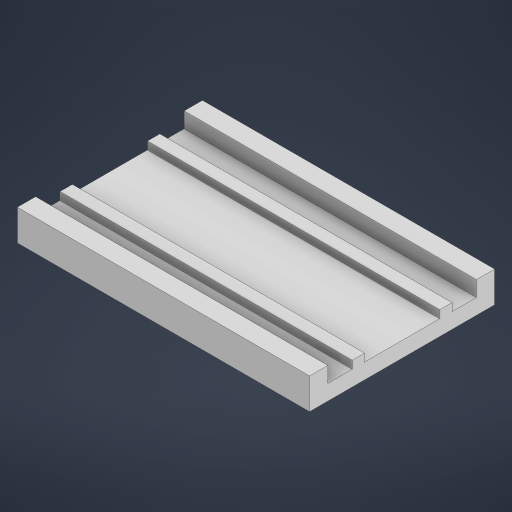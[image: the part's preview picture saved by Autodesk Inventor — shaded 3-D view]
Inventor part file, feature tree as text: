
AUTODESK INVENTOR PART (.ipt)
format: ipt  version: 2024 (Build 280153000, 153)  size: 219,648 bytes
history: native  units: in
note: dims shown in document units (in); Inventor stores cm internally (conversion verified against a paired STEP export)
features: extrude x3, sketch x3
ambient origin geometry x8: Origin, YZ Plane, XZ Plane, XY Plane, X Axis, Y Axis, Z Axis, Center Point
bodies: Solid1 (feature_tree)
feature tree (6):
  extrude  "Extrusion1"  Depth=2.3622in
  extrude  "Extrusion2"  Depth=1.2008in
  extrude  "Extrusion3"  Depth=0.1in
  sketch  "Sketch1"  dims[d0=1.4961in d1=2.3622in]
  sketch  "Sketch2"  dims[d2=0.25in d3=0.0in d4=1.2008in]
  sketch  "Sketch3"  dims[d5=0.125in d6=0.0in d7=0.1in d8=0.1in d9=0.8071in d10=0.4035in d11=0.0625in d12=0.0in]
